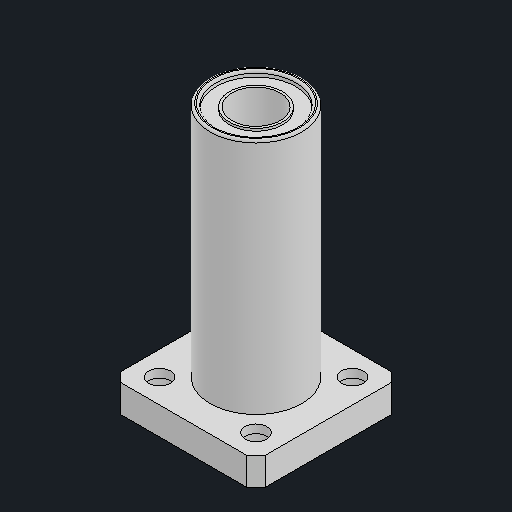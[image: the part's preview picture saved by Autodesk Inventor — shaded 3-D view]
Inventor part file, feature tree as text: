
AUTODESK INVENTOR PART (.ipt)
format: ipt  version: 2024.2 (Build 282272000, 272)  size: 143,872 bytes
history: native  units: mm
features: other x3, fillet x1, extrude x1, chamfer x1
ambient origin geometry x8: Origin, YZ Plane, XZ Plane, XY Plane, X Axis, Y Axis, Z Axis, Center Point
bodies: Body1 (feature_tree), Body2 (feature_tree), Body3 (feature_tree)
feature tree (6):
  other  "솔리드1"
  other  "솔리드2"
  other  "솔리드3"
  fillet  "Fillet1"  [1 undecoded]
  extrude  "Extrude-Thin2"  [1 undecoded]
  chamfer  "Chamfer1"  [1 undecoded]
note: 3 required parameter values undecoded (feature->parameter linkage not recoverable at this tier; creation-order binding heuristic only, values carry confidence <= 0.55)
